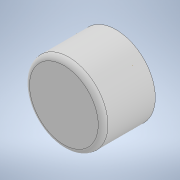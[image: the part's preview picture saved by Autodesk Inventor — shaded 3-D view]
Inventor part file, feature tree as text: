
AUTODESK INVENTOR PART (.ipt)
format: ipt  version: 2021.2 (Build 252289000, 289)  size: 133,120 bytes
history: native  units: in
note: dims shown in document units (in); Inventor stores cm internally (conversion verified against a paired STEP export)
features: sketch x4, extrude x3, fillet x1, plane x1, loft x1, other x1
ambient origin geometry x8: Origin, YZ Plane, XZ Plane, XY Plane, X Axis, Y Axis, Z Axis, Center Point
bodies: Solid1 (feature_tree)
feature tree (11):
  extrude  "Extrusion1"  Depth=0.45in
  extrude  "Extrusion2"  Depth=0.15in
  fillet  "Fillet1"  Radius=0.15in
  plane  "Work Plane1"
  loft  "Loft1"
  extrude  "Extrusion3"  Depth=0.05in
  sketch  "Sketch1"  dims[d0=0.675in d1=0.45in]
  sketch  "Sketch2"  dims[d2=0.0in d3=0.435in d4=0.15in]
  sketch  "Sketch3"  dims[d5=0.0in d6=0.0417in]
  other  "Edges1"
  sketch  "Sketch4"  dims[d7=0.05in d8=0.05in d9=0.0in d10=90.0deg d11=0.0in d12=90.0deg d13=0.075in d14=0.05in d15=0.0in]
